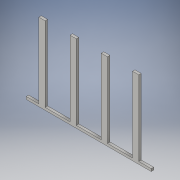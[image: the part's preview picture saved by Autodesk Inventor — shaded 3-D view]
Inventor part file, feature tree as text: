
AUTODESK INVENTOR PART (.ipt)
format: ipt  version: 2016 (Build 200138000, 138)  size: 116,224 bytes
history: native  units: in
note: dims shown in document units (in); Inventor stores cm internally (conversion verified against a paired STEP export)
features: extrude x1, sketch x1
ambient origin geometry x8: Origin, YZ Plane, XZ Plane, XY Plane, X Axis, Y Axis, Z Axis, Center Point
bodies: Solid1 (feature_tree)
feature tree (2):
  extrude  "Extrusion1"  Depth=0.1in
  sketch  "Sketch1"  dims[d0=5.0in d1=0.1in d2=0.5in d3=0.5in d4=0.25in d5=3.0in d6=1.0in d7=0.25in d8=0.25in d9=3.0in d10=1.0in d11=0.25in d12=3.0in d13=0.1in d14=0.0in]
